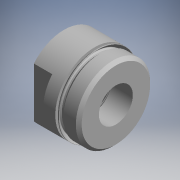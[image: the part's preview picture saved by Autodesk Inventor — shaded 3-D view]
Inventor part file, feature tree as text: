
AUTODESK INVENTOR PART (.ipt)
format: ipt  version: 2017.3 (Build 213256000, 256)  size: 216,576 bytes
history: native  units: mm (DEFAULTED — no unit token found)
features: other x126, sketch x4, revolve x3, thread x1, extrude x1
ambient origin geometry x8: Origin, YZ Plane, XZ Plane, XY Plane, X Axis, Y Axis, Z Axis, Center Point
bodies: Solid1 (feature_tree)
feature tree (135):
  revolve  "Revolution1"  Angle=360.0deg
  revolve  "Revolution2"  [1 undecoded]
  thread  "Thread1"  [1 undecoded]
  extrude  "Extrusion1"  [1 undecoded]
  revolve  "Revolution3"  [1 undecoded]
  other  "cut1_XY"
  other  "cut1_YZ"
  other  "cut1_ZX"
  other  "cut1_X"
  other  "cut1_Y"
  other  "cut1_Z"
  other  "cut1_Center"
  other  "cut2_XY"
  other  "cut2_YZ"
  other  "cut2_ZX"
  other  "cut2_X"
  other  "cut2_Y"
  other  "cut2_Z"
  other  "cut2_Center"
  other  "cutf1_XY"
  other  "cutf1_YZ"
  other  "cutf1_ZX"
  other  "cutf1_X"
  other  "cutf1_Y"
  other  "cutf1_Z"
  other  "cutf1_Center"
  other  "cutf2_XY"
  other  "cutf2_YZ"
  other  "cutf2_ZX"
  other  "cutf2_X"
  other  "cutf2_Y"
  other  "cutf2_Z"
  other  "cutf2_Center"
  other  "lovra_XY"
  other  "lovra_YZ"
  other  "lovra_ZX"
  other  "lovra_X"
  other  "lovra_Y"
  other  "lovra_Z"
  other  "lovra_Center"
  other  "lovra1_XY"
  other  "lovra1_YZ"
  other  "lovra1_ZX"
  other  "lovra1_X"
  other  "lovra1_Y"
  other  "lovra1_Z"
  other  "lovra1_Center"
  other  "lovra2_XY"
  other  "lovra2_YZ"
  other  "lovra2_ZX"
  other  "lovra2_X"
  other  "lovra2_Y"
  other  "lovra2_Z"
  other  "lovra2_Center"
  other  "lovra21_XY"
  other  "lovra21_YZ"
  other  "lovra21_ZX"
  other  "lovra21_X"
  other  "lovra21_Y"
  other  "lovra21_Z"
  other  "lovra21_Center"
  other  "lovra22_XY"
  other  "lovra22_YZ"
  other  "lovra22_ZX"
  other  "lovra22_X"
  other  "lovra22_Y"
  other  "lovra22_Z"
  other  "lovra22_Center"
  other  "lovra3_XY"
  other  "lovra3_YZ"
  other  "lovra3_ZX"
  other  "lovra3_X"
  other  "lovra3_Y"
  other  "lovra3_Z"
  other  "lovra3_Center"
  other  "olen_XY"
  other  "olen_YZ"
  other  "olen_ZX"
  other  "olen_X"
  other  "olen_Y"
  other  "olen_Z"
  other  "olen_Center"
  other  "to_mounting_bracket_XY"
  other  "to_mounting_bracket_YZ"
  other  "to_mounting_bracket_ZX"
  other  "to_mounting_bracket_X"
  other  "to_mounting_bracket_Y"
  other  "to_mounting_bracket_Z"
  other  "to_mounting_bracket_Center"
  other  "to_nut_XY"
  other  "to_nut_YZ"
  other  "to_nut_ZX"
  other  "to_nut_X"
  other  "to_nut_Y"
  other  "to_nut_Z"
  other  "to_nut_Center"
  other  "to_pin_XY"
  other  "to_pin_YZ"
  other  "to_pin_ZX"
  other  "to_pin_X"
  other  "to_pin_Y"
  other  "to_pin_Z"
  other  "to_pin_Center"
  other  "to_pin_1_XY"
  other  "to_pin_1_YZ"
  other  "to_pin_1_ZX"
  other  "to_pin_1_X"
  other  "to_pin_1_Y"
  other  "to_pin_1_Z"
  other  "to_pin_1_Center"
  other  "to_pin_r_XY"
  other  "to_pin_r_YZ"
  other  "to_pin_r_ZX"
  other  "to_pin_r_X"
  other  "to_pin_r_Y"
  other  "to_pin_r_Z"
  other  "to_pin_r_Center"
  other  "to_screw_XY"
  other  "to_screw_YZ"
  other  "to_screw_ZX"
  other  "to_screw_X"
  other  "to_screw_Y"
  other  "to_screw_Z"
  other  "to_screw_Center"
  other  "to_tube_XY"
  other  "to_tube_YZ"
  other  "to_tube_ZX"
  other  "to_tube_X"
  other  "to_tube_Y"
  other  "to_tube_Z"
  other  "to_tube_Center"
  sketch  "Sketch_1"  dims[d0=360.0deg d1=360.0deg]
  sketch  "Sketch_6"  dims[d7=0.0mm d8=0.0mm d9=0.0mm d10=0.0mm d11=0.0mm d12=0.0mm d13=0.0mm d14=0.0mm d15=0.0mm d16=0.0mm]
  sketch  "Sketch_5"  dims[d2=7.03922mm d3=0.0mm d4=4.7752mm d5=0.0mm d6=360.0deg]
  sketch  "Sketch_24"
note: 4 required parameter values undecoded (feature->parameter linkage not recoverable at this tier; creation-order binding heuristic only, values carry confidence <= 0.55)